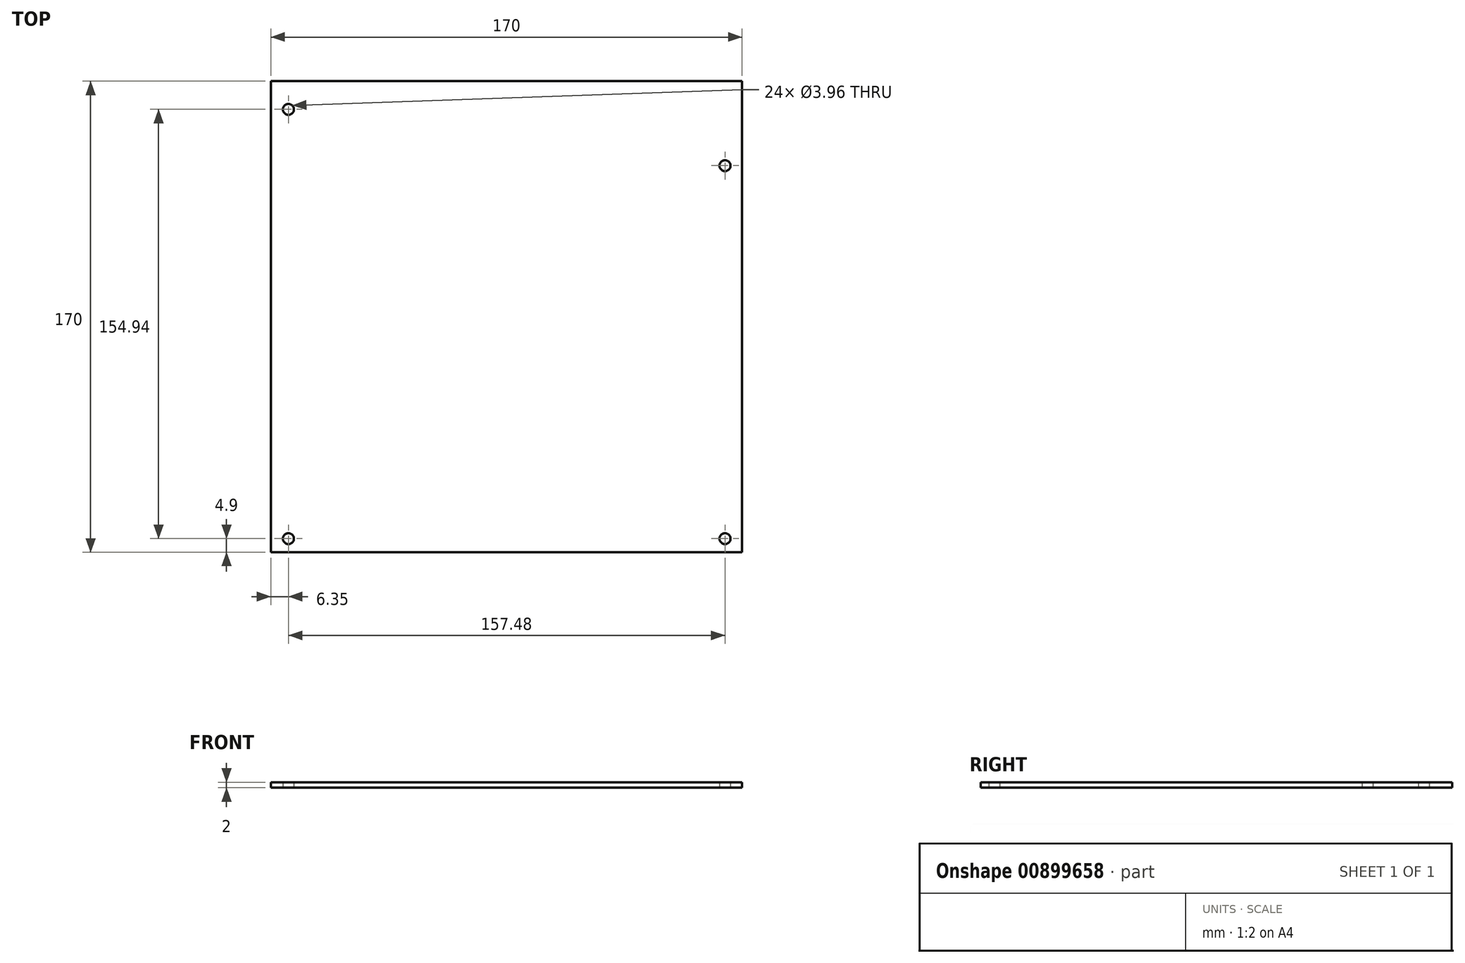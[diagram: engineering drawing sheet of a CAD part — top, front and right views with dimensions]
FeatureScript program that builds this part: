
annotation { "Feature Type Name" : "Feature", "Feature Type Description" : "" }
export const myFeature = defineFeature(function(context is Context, id is Id, definition is map)
    precondition{}
    {
        {
            var Q0;
            Q0=qCreatedBy(makeId("Top.planeOp"),FACE);
            var sketch = newSketch(context, id + "F0", { "sketchPlane" : qUnion([Q0])});
            skLineSegment(sketch, "E0.bottom", {"start": v(-85, 85) * mm, "end": v(85, 85) * mm});
            skLineSegment(sketch, "E0.top", {"start": v(-85, -85) * mm, "end": v(85, -85) * mm});
            skLineSegment(sketch, "E0.left", {"start": v(-85, 85) * mm, "end": v(-85, -85) * mm});
            skLineSegment(sketch, "E0.right", {"start": v(85, 85) * mm, "end": v(85, -85) * mm});
            skPoint(sketch, "E0.middle", {"position": v(0, 0) * mm});
            skCircle(sketch, "E1", {"center": v(-78.65, 74.84) * mm, "radius": 1.98 * mm});
            skCircle(sketch, "E2", {"center": v(-78.65, -80.1) * mm, "radius": 1.98 * mm});
            skCircle(sketch, "E3", {"center": v(78.83, -80.1) * mm, "radius": 1.98 * mm});
            skCircle(sketch, "E4", {"center": v(78.83, 54.52) * mm, "radius": 1.98 * mm});
            skSolve(sketch);
        }
        {
            var Q0;
            Q0=makeQuery(id+"F0.imprint","IMPRINT",FACE,{"disambiguationData":[TD([[makeQuery(id+"F0.imprint","IMPRINT",EDGE,{"derivedFrom":sQuery(id+"F0.wireOp",EDGE,"E0.bottom")}),-1.0]])]});
            extrude(context, id + "F1", {"entities" : qUnion([Q0]), "depth" : 2 * mm, "offsetDistance" : 25 * mm});
        }
    });
